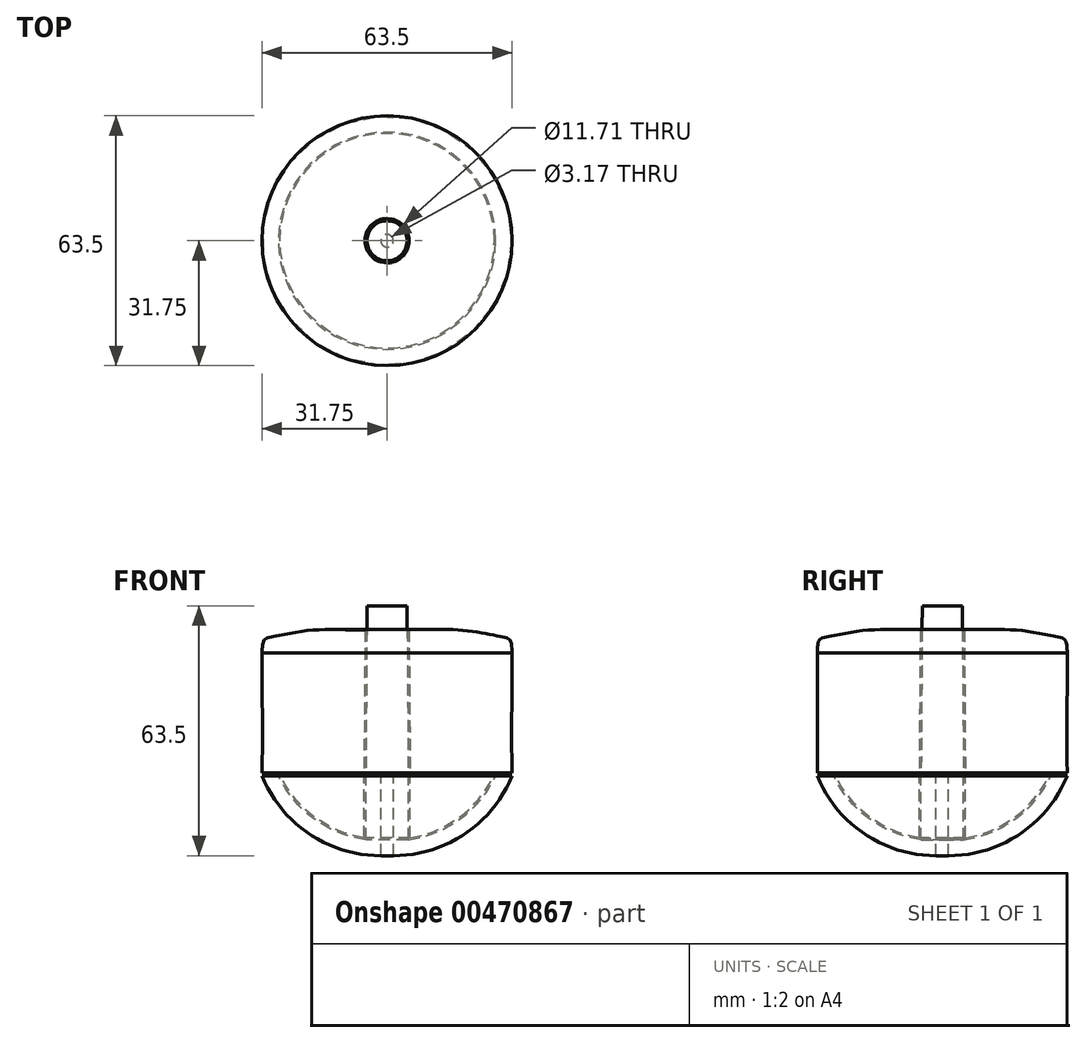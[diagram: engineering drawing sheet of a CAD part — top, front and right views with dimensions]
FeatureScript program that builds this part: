
annotation { "Feature Type Name" : "Feature", "Feature Type Description" : "" }
export const myFeature = defineFeature(function(context is Context, id is Id, definition is map)
    precondition{}
    {
        {
            var Q0;
            Q0=qCreatedBy(makeId("Front.planeOp"),FACE);
            var sketch = newSketch(context, id + "F0", { "sketchPlane" : qUnion([Q0])});
            skLineSegment(sketch, "E0.left", {"start": v(0, 0) * mm, "end": v(0, 63.5) * mm});
            skLineSegment(sketch, "E0.right", {"start": v(63.5, 0) * mm, "end": v(63.5, 63.5) * mm});
            skLineSegment(sketch, "E1", {"start": v(31.75, 0) * mm, "end": v(31.75, -13.3) * mm});
            skLineSegment(sketch, "E2", {"start": v(30.16, 0) * mm, "end": v(33.34, 0) * mm});
            skLineSegment(sketch, "E3", {"start": v(30.16, 0) * mm, "end": v(30.16, 20.27) * mm});
            skLineSegment(sketch, "E4", {"start": v(33.34, 20.32) * mm, "end": v(33.34, 0) * mm});
            skLineSegment(sketch, "E5", {"start": v(30.16, 20.27) * mm, "end": v(33.34, 20.32) * mm});
            skLineSegment(sketch, "E6", {"start": v(26.67, 63.5) * mm, "end": v(63.5, 63.5) * mm});
            skLineSegment(sketch, "E7", {"start": v(31.75, 63.5) * mm, "end": v(26.67, 63.5) * mm});
            skLineSegment(sketch, "E8", {"start": v(31.75, 63.5) * mm, "end": v(31.75, -13.3) * mm});
            skArc(sketch, "E9", {"start": v(0, 20.27) * mm, "mid": v(12, 5.54) * mm, "end": v(30.16, 0) * mm});
            skLineSegment(sketch, "E10.0", {"start": v(26.35, 4.06) * mm, "end": v(26.35, 20.27) * mm});
            skArc(sketch, "E10.1", {"start": v(4.16, 20.27) * mm, "mid": v(13.2, 9.35) * mm, "end": v(26.35, 4.06) * mm});
            skLineSegment(sketch, "E11", {"start": v(0, 20.27) * mm, "end": v(4.16, 20.27) * mm});
            skLineSegment(sketch, "E12.0", {"start": v(25.9, 4.6) * mm, "end": v(25.9, 20.32) * mm});
            skArc(sketch, "E12.1", {"start": v(4.47, 20.68) * mm, "mid": v(13.16, 9.94) * mm, "end": v(25.9, 4.6) * mm});
            skLineSegment(sketch, "E13", {"start": v(4.47, 20.68) * mm, "end": v(25.9, 20.32) * mm});
            skLineSegment(sketch, "E14", {"start": v(26.67, 63.5) * mm, "end": v(26.35, 20.27) * mm});
            skLineSegment(sketch, "E15", {"start": v(0, 21.1) * mm, "end": v(25.9, 20.9) * mm});
            skLineSegment(sketch, "E16", {"start": v(25.9, 20.9) * mm, "end": v(26.16, 57.32) * mm});
            skPoint(sketch, "E17.1.internal.snap0", {"position": v(12.95, 21) * mm});
            skFitSpline(sketch, "E17", {"points": [v(26.16, 57.32) * mm, v(12.95, 57.32) * mm, v(3.15, 55.76) * mm, v(0.7, 54.97) * mm, v(0, 51.56) * mm, v(0, 21.1) * mm], "startDerivative": vector(-55.27, 0.21) * mm, "endDerivative": vector(-2.2, -113.47) * mm});
            skLineSegment(sketch, "E18.MirrorCS", {"start": v(59.03, 20.68) * mm, "end": v(37.6, 20.32) * mm});
            skLineSegment(sketch, "E19.MirrorCS", {"start": v(37.6, 4.6) * mm, "end": v(37.6, 20.32) * mm});
            skArc(sketch, "E20.MirrorCS", {"start": v(59.03, 20.68) * mm, "mid": v(50.34, 9.94) * mm, "end": v(37.6, 4.6) * mm});
            skSolve(sketch);
        }
        {
            var Q0;
            {var subQ1=sQuery(id+"F0.wireOp",EDGE,"E15");Q0=makeQuery(id+"F0.imprint","IMPRINT",FACE,{"disambiguationData":[TD([[makeQuery(id+"F0.imprint","IMPRINT",EDGE,{"derivedFrom":subQ1}),1.0]])]});}
            var Q1;
            Q1=sQuery(id+"F0.wireOp",EDGE,"E8");
            revolve(context, id + "F1", {"entities" : qUnion([Q0]), "axis" : qUnion([Q1]), "revolveType" : RevolveType.FULL});
        }
        {
            var Q0;
            Q0=makeQuery(id+"F0.imprint","IMPRINT",FACE,{"disambiguationData":[TD([[makeQuery(id+"F0.imprint","IMPRINT",EDGE,{"derivedFrom":sQuery(id+"F0.wireOp",EDGE,"E12.0")}),1.0]])]});
            var Q1;
            Q1=sQuery(id+"F0.wireOp",EDGE,"E8");
            revolve(context, id + "F2", {"entities" : qUnion([Q0]), "axis" : qUnion([Q1]), "revolveType" : RevolveType.FULL});
        }
        {
            var Q0;
            {var subQ2=sQuery(id+"F0.wireOp",EDGE,"E3");Q0=makeQuery(id+"F0.imprint","IMPRINT",FACE,{"disambiguationData":[TD([[makeQuery(id+"F0.imprint","IMPRINT",EDGE,{"derivedFrom":subQ2}),1.0]])]});}
            var Q1;
            Q1=sQuery(id+"F0.wireOp",EDGE,"E8");
            revolve(context, id + "F3", {"entities" : qUnion([Q0]), "axis" : qUnion([Q1]), "revolveType" : RevolveType.FULL});
        }
    });
